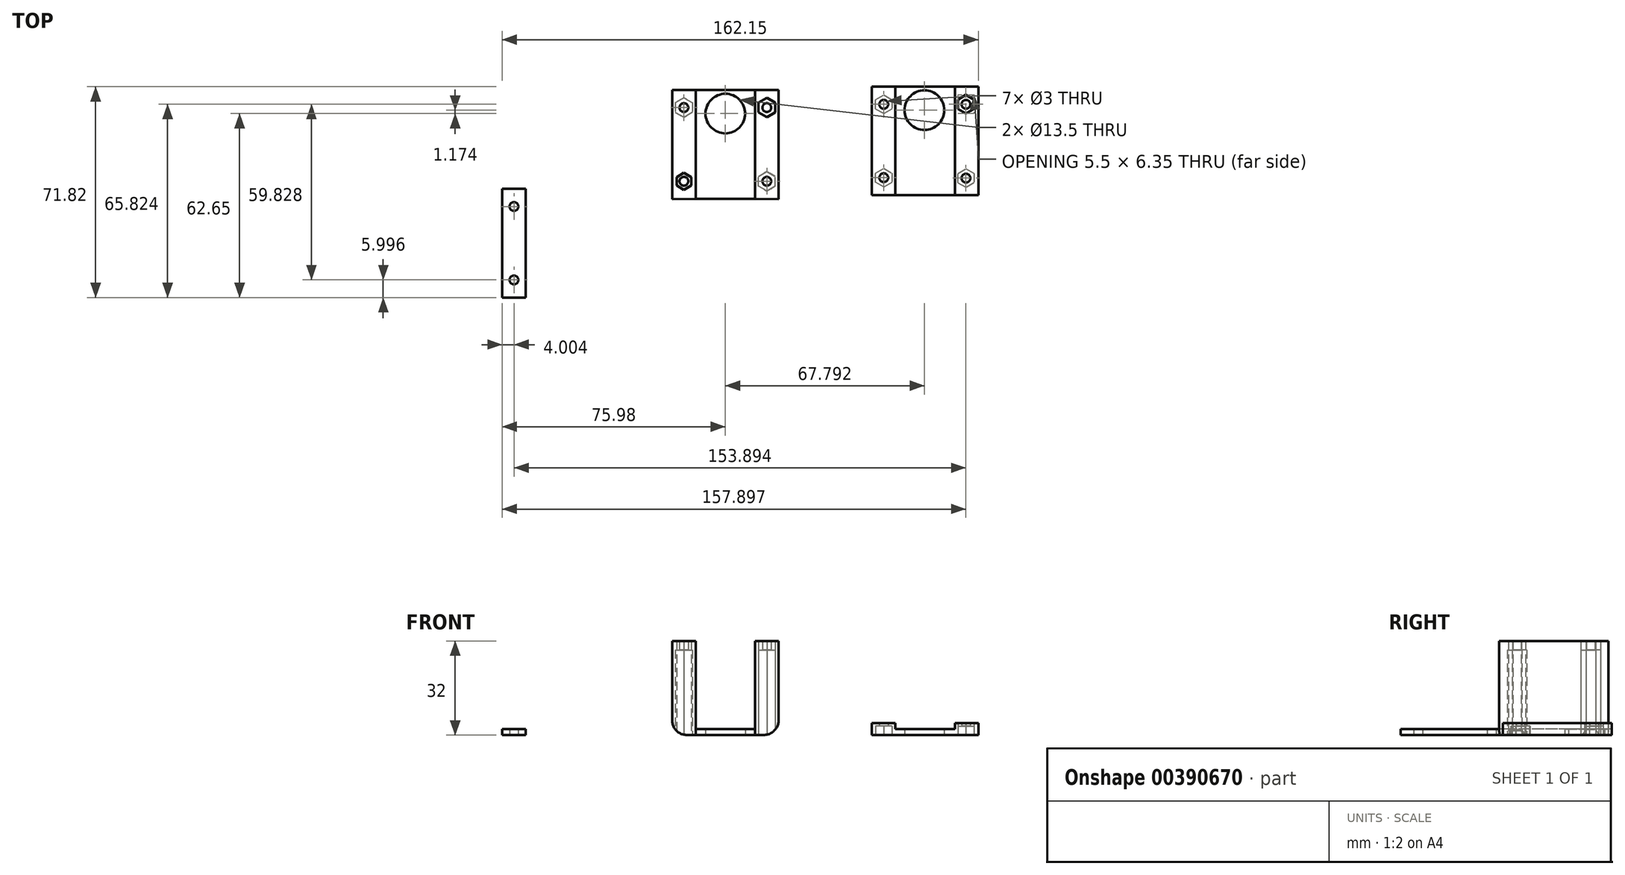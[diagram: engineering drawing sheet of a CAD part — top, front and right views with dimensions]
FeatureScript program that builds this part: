
annotation { "Feature Type Name" : "Feature", "Feature Type Description" : "" }
export const myFeature = defineFeature(function(context is Context, id is Id, definition is map)
    precondition{}
    {
        {
            var Q0;
            Q0=qCreatedBy(makeId("Top.planeOp"),FACE);
            var sketch = newSketch(context, id + "F0", { "sketchPlane" : qUnion([Q0])});
            skLineSegment(sketch, "E0.bottom", {"start": v(10.13, 18.5) * mm, "end": v(-10.12, 18.5) * mm});
            skLineSegment(sketch, "E0.top", {"start": v(10.12, -18.5) * mm, "end": v(-10.13, -18.5) * mm});
            skLineSegment(sketch, "E0.left", {"start": v(10.13, 18.5) * mm, "end": v(10.12, -18.5) * mm});
            skLineSegment(sketch, "E0.right", {"start": v(-10.12, 18.5) * mm, "end": v(-10.12, -18.5) * mm});
            skPoint(sketch, "E0.middle", {"position": v(0, 0) * mm});
            skCircle(sketch, "E1", {"center": v(0, 10.5) * mm, "radius": 6.75 * mm});
            skLineSegment(sketch, "E2.0", {"start": v(-18.12, 18.6) * mm, "end": v(-18.12, -18.6) * mm});
            skLineSegment(sketch, "E3.0", {"start": v(18.13, 18.6) * mm, "end": v(18.13, -18.6) * mm});
            skLineSegment(sketch, "E4", {"start": v(-18.13, 18.6) * mm, "end": v(-10.12, 18.5) * mm});
            skLineSegment(sketch, "E5", {"start": v(10.13, 18.5) * mm, "end": v(18.13, 18.6) * mm});
            skLineSegment(sketch, "E6", {"start": v(18.13, -18.6) * mm, "end": v(10.12, -18.5) * mm});
            skLineSegment(sketch, "E7", {"start": v(-10.12, -18.5) * mm, "end": v(-18.12, -18.6) * mm});
            skCircle(sketch, "E8", {"center": v(-14.12, 12.55) * mm, "radius": 1.5 * mm});
            skCircle(sketch, "E9.MirrorC", {"center": v(-14.12, -12.55) * mm, "radius": 1.5 * mm});
            skCircle(sketch, "E10.MirrorC", {"center": v(14.12, -12.55) * mm, "radius": 1.5 * mm});
            skCircle(sketch, "E11.MirrorC", {"center": v(14.12, 12.55) * mm, "radius": 1.5 * mm});
            skCircle(sketch, "E12.cCircle", {"center": v(-14.12, 12.55) * mm, "radius": 3.32 * mm, "construction": true});
            skLineSegment(sketch, "E12.0", {"start": v(-14.12, 15.87) * mm, "end": v(-11.25, 14.21) * mm});
            skLineSegment(sketch, "E12.1", {"start": v(-11.25, 14.21) * mm, "end": v(-11.25, 10.9) * mm});
            skLineSegment(sketch, "E12.2", {"start": v(-11.25, 10.9) * mm, "end": v(-14.12, 9.23) * mm});
            skLineSegment(sketch, "E12.3", {"start": v(-14.12, 9.23) * mm, "end": v(-17, 10.9) * mm});
            skLineSegment(sketch, "E12.4", {"start": v(-17, 10.9) * mm, "end": v(-17, 14.21) * mm});
            skLineSegment(sketch, "E12.5", {"start": v(-17, 14.21) * mm, "end": v(-14.12, 15.87) * mm});
            skCircle(sketch, "E13.cCircle", {"center": v(14.12, 12.55) * mm, "radius": 3.32 * mm, "construction": true});
            skLineSegment(sketch, "E13.0", {"start": v(14.12, 15.87) * mm, "end": v(17, 14.21) * mm});
            skLineSegment(sketch, "E13.1", {"start": v(17, 14.21) * mm, "end": v(17, 10.9) * mm});
            skLineSegment(sketch, "E13.2", {"start": v(17, 10.9) * mm, "end": v(14.13, 9.23) * mm});
            skLineSegment(sketch, "E13.3", {"start": v(14.13, 9.23) * mm, "end": v(11.25, 10.9) * mm});
            skLineSegment(sketch, "E13.4", {"start": v(11.25, 10.9) * mm, "end": v(11.25, 14.21) * mm});
            skLineSegment(sketch, "E13.5", {"start": v(11.25, 14.21) * mm, "end": v(14.12, 15.87) * mm});
            skCircle(sketch, "E14.cCircle", {"center": v(14.12, -12.55) * mm, "radius": 3.32 * mm, "construction": true});
            skLineSegment(sketch, "E14.0", {"start": v(14.12, -9.23) * mm, "end": v(17, -10.9) * mm});
            skLineSegment(sketch, "E14.1", {"start": v(17, -10.9) * mm, "end": v(17, -14.21) * mm});
            skLineSegment(sketch, "E14.2", {"start": v(17, -14.21) * mm, "end": v(14.12, -15.87) * mm});
            skLineSegment(sketch, "E14.3", {"start": v(14.12, -15.87) * mm, "end": v(11.25, -14.21) * mm});
            skLineSegment(sketch, "E14.4", {"start": v(11.25, -14.21) * mm, "end": v(11.25, -10.9) * mm});
            skLineSegment(sketch, "E14.5", {"start": v(11.25, -10.9) * mm, "end": v(14.12, -9.23) * mm});
            skCircle(sketch, "E15.cCircle", {"center": v(-14.12, -12.55) * mm, "radius": 2.88 * mm, "construction": true});
            skLineSegment(sketch, "E15.0", {"start": v(-14.12, -9.68) * mm, "end": v(-11.64, -11.11) * mm});
            skLineSegment(sketch, "E15.1", {"start": v(-11.64, -11.11) * mm, "end": v(-11.64, -13.99) * mm});
            skLineSegment(sketch, "E15.2", {"start": v(-11.64, -13.99) * mm, "end": v(-14.12, -15.43) * mm});
            skLineSegment(sketch, "E15.3", {"start": v(-14.12, -15.43) * mm, "end": v(-16.61, -13.99) * mm});
            skLineSegment(sketch, "E15.4", {"start": v(-16.61, -13.99) * mm, "end": v(-16.61, -11.11) * mm});
            skLineSegment(sketch, "E15.5", {"start": v(-16.61, -11.11) * mm, "end": v(-14.12, -9.68) * mm});
            skSolve(sketch);
        }
        {
            var Q0;
            Q0=makeQuery(id+"F0.imprint","IMPRINT",FACE,{"disambiguationData":[TD([[makeQuery(id+"F0.imprint","IMPRINT",EDGE,{"derivedFrom":sQuery(id+"F0.wireOp",EDGE,"E0.bottom")}),1.0]])]});
            extrude(context, id + "F1", {"entities" : qUnion([Q0]), "depth" : 2 * mm});
        }
        {
            var Q0;
            Q0=makeQuery(id+"F0.imprint","IMPRINT",FACE,{"disambiguationData":[TD([[makeQuery(id+"F0.imprint","IMPRINT",EDGE,{"derivedFrom":sQuery(id+"F0.wireOp",EDGE,"E0.right")}),-1.0]])]});
            var Q1;
            Q1=makeQuery(id+"F0.imprint","IMPRINT",FACE,{"disambiguationData":[TD([[makeQuery(id+"F0.imprint","IMPRINT",EDGE,{"derivedFrom":sQuery(id+"F0.wireOp",EDGE,"E0.left")}),1.0]])]});
            var Q2;
            Q2=makeQuery(id+"F0.imprint","IMPRINT",FACE,{"disambiguationData":[TD([[makeQuery(id+"F0.imprint","IMPRINT",EDGE,{"derivedFrom":sQuery(id+"F0.wireOp",EDGE,"E10.MirrorC")}),-1.0]])]});
            var Q3;
            Q3=makeQuery(id+"F0.imprint","IMPRINT",FACE,{"disambiguationData":[TD([[makeQuery(id+"F0.imprint","IMPRINT",EDGE,{"derivedFrom":sQuery(id+"F0.wireOp",EDGE,"E9.MirrorC")}),1.0]])]});
            var Q4;
            Q4=makeQuery(id+"F0.imprint","IMPRINT",FACE,{"disambiguationData":[TD([[makeQuery(id+"F0.imprint","IMPRINT",EDGE,{"derivedFrom":sQuery(id+"F0.wireOp",EDGE,"E8")}),-1.0]])]});
            var Q5;
            Q5=makeQuery(id+"F0.imprint","IMPRINT",FACE,{"disambiguationData":[TD([[makeQuery(id+"F0.imprint","IMPRINT",EDGE,{"derivedFrom":sQuery(id+"F0.wireOp",EDGE,"E11.MirrorC")}),1.0]])]});
            extrude(context, id + "F2", {"entities" : qUnion([Q0, Q1, Q2, Q3, Q4, Q5]), "operationType" : NewBodyOperationType.ADD, "depth" : 32 * mm});
        }
        {
            var Q0;
            Q0=makeQuery(id+"F0.imprint","IMPRINT",FACE,{"disambiguationData":[TD([[makeQuery(id+"F0.imprint","IMPRINT",EDGE,{"derivedFrom":sQuery(id+"F0.wireOp",EDGE,"E10.MirrorC")}),-1.0]])]});
            var Q1;
            Q1=makeQuery(id+"F0.imprint","IMPRINT",FACE,{"disambiguationData":[TD([[makeQuery(id+"F0.imprint","IMPRINT",EDGE,{"derivedFrom":sQuery(id+"F0.wireOp",EDGE,"E11.MirrorC")}),1.0]])]});
            var Q2;
            Q2=makeQuery(id+"F0.imprint","IMPRINT",FACE,{"disambiguationData":[TD([[makeQuery(id+"F0.imprint","IMPRINT",EDGE,{"derivedFrom":sQuery(id+"F0.wireOp",EDGE,"E8")}),-1.0]])]});
            var Q3;
            Q3=makeQuery(id+"F0.imprint","IMPRINT",FACE,{"disambiguationData":[TD([[makeQuery(id+"F0.imprint","IMPRINT",EDGE,{"derivedFrom":sQuery(id+"F0.wireOp",EDGE,"E9.MirrorC")}),1.0]])]});
            extrude(context, id + "F3", {"entities" : qUnion([Q0, Q1, Q2, Q3]), "operationType" : NewBodyOperationType.REMOVE, "depth" : 29 * mm});
        }
        {
            var Q0;
            Q0=qCreatedBy(makeId("Top.planeOp"),FACE);
            var sketch = newSketch(context, id + "F4", { "sketchPlane" : qUnion([Q0])});
            skLineSegment(sketch, "E16.bottom", {"start": v(78.17, 19.67) * mm, "end": v(57.92, 19.67) * mm});
            skLineSegment(sketch, "E16.top", {"start": v(78.17, -17.33) * mm, "end": v(57.92, -17.33) * mm});
            skLineSegment(sketch, "E16.left", {"start": v(78.17, 19.67) * mm, "end": v(78.17, -17.33) * mm});
            skLineSegment(sketch, "E16.right", {"start": v(57.92, 19.67) * mm, "end": v(57.92, -17.33) * mm});
            skPoint(sketch, "E16.middle", {"position": v(68.05, 1.17) * mm});
            skCircle(sketch, "E17", {"center": v(67.8, 11.67) * mm, "radius": 6.75 * mm});
            skLineSegment(sketch, "E18.0", {"start": v(49.92, 19.67) * mm, "end": v(49.92, -17.33) * mm});
            skLineSegment(sketch, "E19.0", {"start": v(86.17, 19.67) * mm, "end": v(86.17, -17.33) * mm});
            skLineSegment(sketch, "E20", {"start": v(49.92, 19.67) * mm, "end": v(57.92, 19.67) * mm});
            skLineSegment(sketch, "E21", {"start": v(78.17, 19.67) * mm, "end": v(86.17, 19.67) * mm});
            skLineSegment(sketch, "E22", {"start": v(86.17, -17.33) * mm, "end": v(78.17, -17.33) * mm});
            skLineSegment(sketch, "E23", {"start": v(57.92, -17.33) * mm, "end": v(49.92, -17.33) * mm});
            skCircle(sketch, "E24", {"center": v(53.92, 13.67) * mm, "radius": 1.5 * mm});
            skCircle(sketch, "E25.MirrorC", {"center": v(81.92, -11.47) * mm, "radius": 1.5 * mm});
            skCircle(sketch, "E26.MirrorC", {"center": v(81.92, 13.67) * mm, "radius": 1.5 * mm});
            skCircle(sketch, "E27.cCircle", {"center": v(53.92, 13.67) * mm, "radius": 2.75 * mm, "construction": true});
            skLineSegment(sketch, "E27.0", {"start": v(51.17, 12.09) * mm, "end": v(51.17, 15.26) * mm});
            skLineSegment(sketch, "E27.1", {"start": v(51.17, 15.26) * mm, "end": v(53.92, 16.85) * mm});
            skLineSegment(sketch, "E27.2", {"start": v(53.92, 16.85) * mm, "end": v(56.67, 15.26) * mm});
            skLineSegment(sketch, "E27.3", {"start": v(56.67, 15.26) * mm, "end": v(56.67, 12.09) * mm});
            skLineSegment(sketch, "E27.4", {"start": v(56.67, 12.09) * mm, "end": v(53.92, 10.5) * mm});
            skLineSegment(sketch, "E27.5", {"start": v(53.92, 10.5) * mm, "end": v(51.17, 12.09) * mm});
            skPoint(sketch, "E27.0.midPoint", {"position": v(51.17, 13.67) * mm});
            skCircle(sketch, "E28.cCircle", {"center": v(81.92, 13.67) * mm, "radius": 2.75 * mm, "construction": true});
            skLineSegment(sketch, "E28.0", {"start": v(84.67, 15.26) * mm, "end": v(84.67, 12.09) * mm});
            skLineSegment(sketch, "E28.1", {"start": v(84.67, 12.09) * mm, "end": v(81.92, 10.5) * mm});
            skLineSegment(sketch, "E28.2", {"start": v(81.92, 10.5) * mm, "end": v(79.17, 12.09) * mm});
            skLineSegment(sketch, "E28.3", {"start": v(79.17, 12.09) * mm, "end": v(79.17, 15.26) * mm});
            skLineSegment(sketch, "E28.4", {"start": v(79.17, 15.26) * mm, "end": v(81.92, 16.85) * mm});
            skLineSegment(sketch, "E28.5", {"start": v(81.92, 16.85) * mm, "end": v(84.67, 15.26) * mm});
            skPoint(sketch, "E28.0.midPoint", {"position": v(84.67, 13.67) * mm});
            skCircle(sketch, "E29.cCircle", {"center": v(81.92, -11.47) * mm, "radius": 2.75 * mm, "construction": true});
            skLineSegment(sketch, "E29.0", {"start": v(84.67, -9.88) * mm, "end": v(84.67, -13.06) * mm});
            skLineSegment(sketch, "E29.1", {"start": v(84.67, -13.06) * mm, "end": v(81.92, -14.64) * mm});
            skLineSegment(sketch, "E29.2", {"start": v(81.92, -14.64) * mm, "end": v(79.17, -13.06) * mm});
            skLineSegment(sketch, "E29.3", {"start": v(79.17, -13.06) * mm, "end": v(79.17, -9.88) * mm});
            skLineSegment(sketch, "E29.4", {"start": v(79.17, -9.88) * mm, "end": v(81.92, -8.3) * mm});
            skLineSegment(sketch, "E29.5", {"start": v(81.92, -8.3) * mm, "end": v(84.67, -9.88) * mm});
            skPoint(sketch, "E29.0.midPoint", {"position": v(84.67, -11.47) * mm});
            skCircle(sketch, "E30.cCircle", {"center": v(53.92, -11.33) * mm, "radius": 2.75 * mm, "construction": true});
            skLineSegment(sketch, "E30.0", {"start": v(51.17, -12.91) * mm, "end": v(51.17, -9.74) * mm});
            skLineSegment(sketch, "E30.1", {"start": v(51.17, -9.74) * mm, "end": v(53.92, -8.15) * mm});
            skLineSegment(sketch, "E30.2", {"start": v(53.92, -8.15) * mm, "end": v(56.67, -9.74) * mm});
            skLineSegment(sketch, "E30.3", {"start": v(56.67, -9.74) * mm, "end": v(56.67, -12.91) * mm});
            skLineSegment(sketch, "E30.4", {"start": v(56.67, -12.91) * mm, "end": v(53.92, -14.5) * mm});
            skLineSegment(sketch, "E30.5", {"start": v(53.92, -14.5) * mm, "end": v(51.17, -12.91) * mm});
            skPoint(sketch, "E30.0.midPoint", {"position": v(51.17, -11.33) * mm});
            skCircle(sketch, "E31", {"center": v(53.92, -11.33) * mm, "radius": 1.5 * mm});
            skSolve(sketch);
        }
        {
            var Q0;
            Q0=makeQuery(id+"F4.imprint","IMPRINT",FACE,{"disambiguationData":[TD([[makeQuery(id+"F4.imprint","IMPRINT",EDGE,{"derivedFrom":sQuery(id+"F4.wireOp",EDGE,"E16.bottom")}),1.0]])]});
            extrude(context, id + "F5", {"entities" : qUnion([Q0]), "depth" : 2 * mm});
        }
        {
            var Q0;
            Q0=qCreatedBy(makeId("Top.planeOp"),FACE);
            var sketch = newSketch(context, id + "F6", { "sketchPlane" : qUnion([Q0])});
            skLineSegment(sketch, "E32.right", {"start": v(-67.98, -15.15) * mm, "end": v(-67.98, -52.15) * mm});
            skLineSegment(sketch, "E33.0", {"start": v(-75.98, -15.15) * mm, "end": v(-75.98, -52.15) * mm});
            skLineSegment(sketch, "E34", {"start": v(-75.98, -15.15) * mm, "end": v(-67.98, -15.15) * mm});
            skLineSegment(sketch, "E35", {"start": v(-67.98, -52.15) * mm, "end": v(-75.98, -52.15) * mm});
            skCircle(sketch, "E36", {"center": v(-71.98, -21.15) * mm, "radius": 1.5 * mm});
            skCircle(sketch, "E37.MirrorC", {"center": v(-71.98, -46.15) * mm, "radius": 1.5 * mm});
            skSolve(sketch);
        }
        {
            var Q0;
            Q0=makeQuery(id+"F6.imprint","IMPRINT",FACE,{"disambiguationData":[TD([[makeQuery(id+"F6.imprint","IMPRINT",EDGE,{"derivedFrom":sQuery(id+"F6.wireOp",EDGE,"E32.right")}),-1.0]])]});
            extrude(context, id + "F7", {"entities" : qUnion([Q0]), "depth" : 2 * mm});
        }
        {
            var Q0;
            Q0=makeQuery(id+"F4.imprint","IMPRINT",FACE,{"disambiguationData":[TD([[makeQuery(id+"F4.imprint","IMPRINT",EDGE,{"derivedFrom":sQuery(id+"F4.wireOp",EDGE,"E16.right")}),-1.0]])]});
            var Q1;
            Q1=makeQuery(id+"F4.imprint","IMPRINT",FACE,{"disambiguationData":[TD([[makeQuery(id+"F4.imprint","IMPRINT",EDGE,{"derivedFrom":sQuery(id+"F4.wireOp",EDGE,"E16.left")}),1.0]])]});
            var Q2;
            Q2=makeQuery(id+"F4.imprint","IMPRINT",FACE,{"disambiguationData":[TD([[makeQuery(id+"F4.imprint","IMPRINT",EDGE,{"derivedFrom":sQuery(id+"F4.wireOp",EDGE,"E30.0")}),-1.0]])]});
            var Q3;
            Q3=makeQuery(id+"F4.imprint","IMPRINT",FACE,{"disambiguationData":[TD([[makeQuery(id+"F4.imprint","IMPRINT",EDGE,{"derivedFrom":sQuery(id+"F4.wireOp",EDGE,"E24")}),-1.0]])]});
            var Q4;
            Q4=makeQuery(id+"F4.imprint","IMPRINT",FACE,{"disambiguationData":[TD([[makeQuery(id+"F4.imprint","IMPRINT",EDGE,{"derivedFrom":sQuery(id+"F4.wireOp",EDGE,"E25.MirrorC")}),-1.0]])]});
            var Q5;
            Q5=makeQuery(id+"F4.imprint","IMPRINT",FACE,{"disambiguationData":[TD([[makeQuery(id+"F4.imprint","IMPRINT",EDGE,{"derivedFrom":sQuery(id+"F4.wireOp",EDGE,"E26.MirrorC")}),1.0]])]});
            extrude(context, id + "F8", {"entities" : qUnion([Q0, Q1, Q2, Q3, Q4, Q5]), "operationType" : NewBodyOperationType.ADD, "depth" : 4 * mm});
        }
        {
            var Q0;
            Q0=makeQuery(id+"F4.imprint","IMPRINT",FACE,{"disambiguationData":[TD([[makeQuery(id+"F4.imprint","IMPRINT",EDGE,{"derivedFrom":sQuery(id+"F4.wireOp",EDGE,"E24")}),-1.0]])]});
            var Q1;
            Q1=makeQuery(id+"F4.imprint","IMPRINT",FACE,{"disambiguationData":[TD([[makeQuery(id+"F4.imprint","IMPRINT",EDGE,{"derivedFrom":sQuery(id+"F4.wireOp",EDGE,"E26.MirrorC")}),1.0]])]});
            var Q2;
            Q2=makeQuery(id+"F4.imprint","IMPRINT",FACE,{"disambiguationData":[TD([[makeQuery(id+"F4.imprint","IMPRINT",EDGE,{"derivedFrom":sQuery(id+"F4.wireOp",EDGE,"E25.MirrorC")}),-1.0]])]});
            var Q3;
            Q3=makeQuery(id+"F4.imprint","IMPRINT",FACE,{"disambiguationData":[TD([[makeQuery(id+"F4.imprint","IMPRINT",EDGE,{"derivedFrom":sQuery(id+"F4.wireOp",EDGE,"E30.0")}),-1.0]])]});
            extrude(context, id + "F9", {"entities" : qUnion([Q0, Q1, Q2, Q3]), "operationType" : NewBodyOperationType.REMOVE, "depth" : 3 * mm});
        }
        {
            var Q0;
            Q0=makeQuery(id+"F2.opExtrude","CAP_EDGE",EDGE,{"disambiguationData":[OSD([sQuery(id+"F0.wireOp",EDGE,"E2.0")])],"isStart":true});
            var Q1;
            Q1=makeQuery(id+"F2.opExtrude","CAP_EDGE",EDGE,{"disambiguationData":[OSD([sQuery(id+"F0.wireOp",EDGE,"E3.0")])],"isStart":true});
            fillet(context, id + "F10", {"entities" : qUnion([Q0, Q1]), "radius" : 5 * mm, "allowEdgeOverflow" : false});
        }
    });
